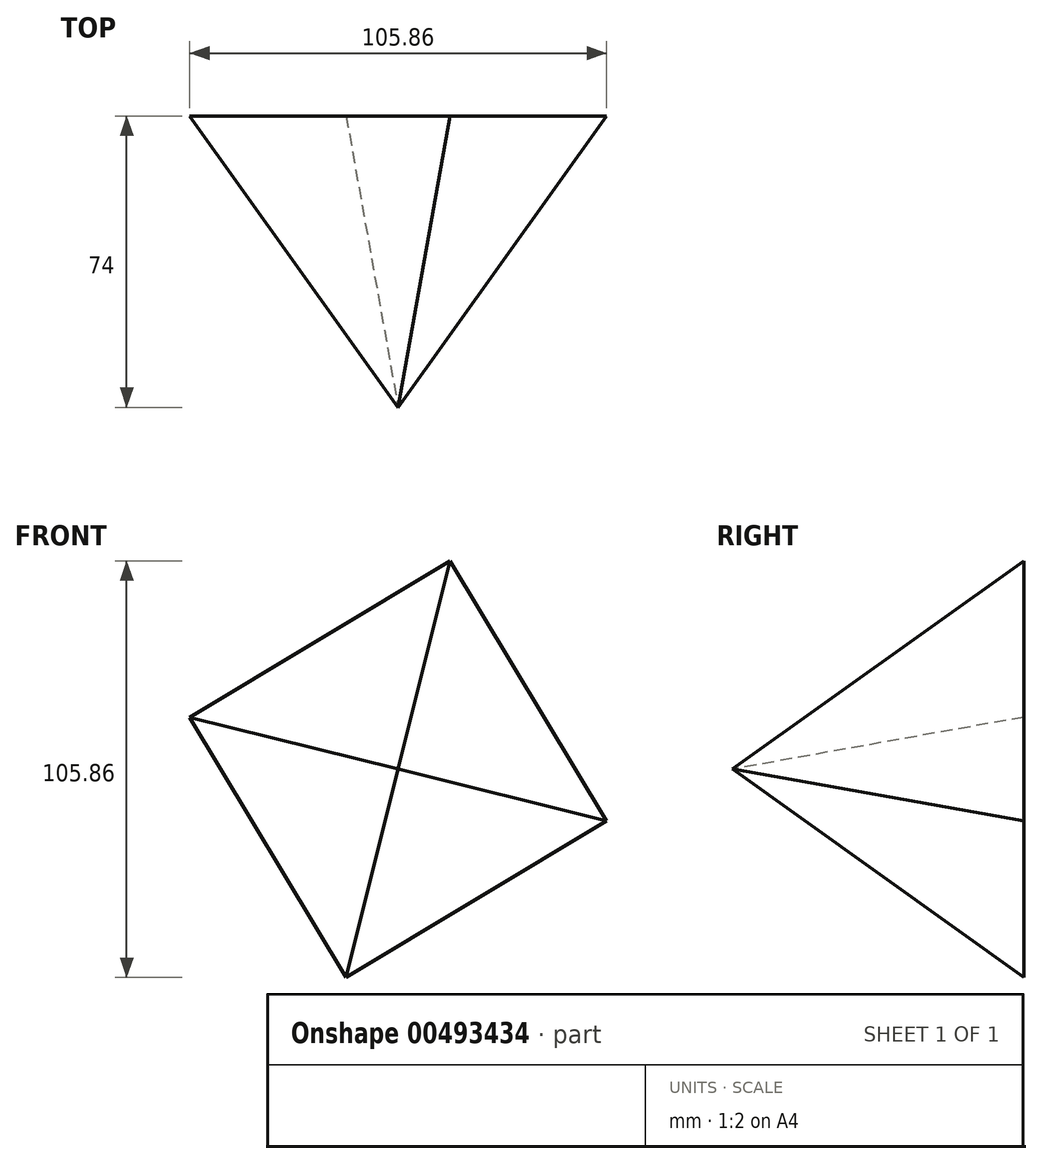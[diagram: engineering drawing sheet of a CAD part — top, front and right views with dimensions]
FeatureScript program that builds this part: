
annotation { "Feature Type Name" : "Feature", "Feature Type Description" : "" }
export const myFeature = defineFeature(function(context is Context, id is Id, definition is map)
    precondition{}
    {
        {
            var Q0;
            Q0=qCreatedBy(makeId("Front.planeOp"),FACE);
            var sketch = newSketch(context, id + "F0", { "sketchPlane" : qUnion([Q0])});
            skCircle(sketch, "E0.cCircle", {"center": v(0, 0) * mm, "radius": 54.55 * mm, "construction": true});
            skLineSegment(sketch, "E0.0", {"start": v(13.2, 52.93) * mm, "end": v(52.93, -13.2) * mm});
            skLineSegment(sketch, "E0.1", {"start": v(52.93, -13.2) * mm, "end": v(-13.2, -52.93) * mm});
            skLineSegment(sketch, "E0.2", {"start": v(-13.2, -52.93) * mm, "end": v(-52.93, 13.2) * mm});
            skLineSegment(sketch, "E0.3", {"start": v(-52.93, 13.2) * mm, "end": v(13.2, 52.93) * mm});
            skSolve(sketch);
        }
        {
            var Q0;
            Q0=qCreatedBy(makeId("Front.planeOp"),FACE);
            cPlane(context, id + "F1", {"entities" : qUnion([Q0]), "cplaneType" : CPlaneType.OFFSET, "offset" : 74 * mm, "width" : 150 * mm, "height" : 150 * mm});
        }
        {
            var Q0;
            Q0=qCreatedBy(id+"F1.planeOp",FACE);
            var sketch = newSketch(context, id + "F2", { "sketchPlane" : qUnion([Q0])});
            skCircle(sketch, "E1", {"center": v(0, 0) * mm, "radius": 4.33 * mm});
            skSolve(sketch);
        }
        {
            var Q0;
            Q0=makeQuery(id+"F0.imprint","IMPRINT",FACE,{"disambiguationData":[TD([[makeQuery(id+"F0.imprint","IMPRINT",EDGE,{"derivedFrom":sQuery(id+"F0.wireOp",EDGE,"E0.0")}),-1.0]])]});
            var Q1;
            Q1=sQuery(id+"F2.wireOp",VERTEX,"E1.center");
            loft(context, id + "F3", {"sheetProfilesArray" : [{ "sheetProfileEntities" : qUnion([Q0]) }, { "sheetProfileEntities" : qUnion([Q1]) }]});
        }
    });
